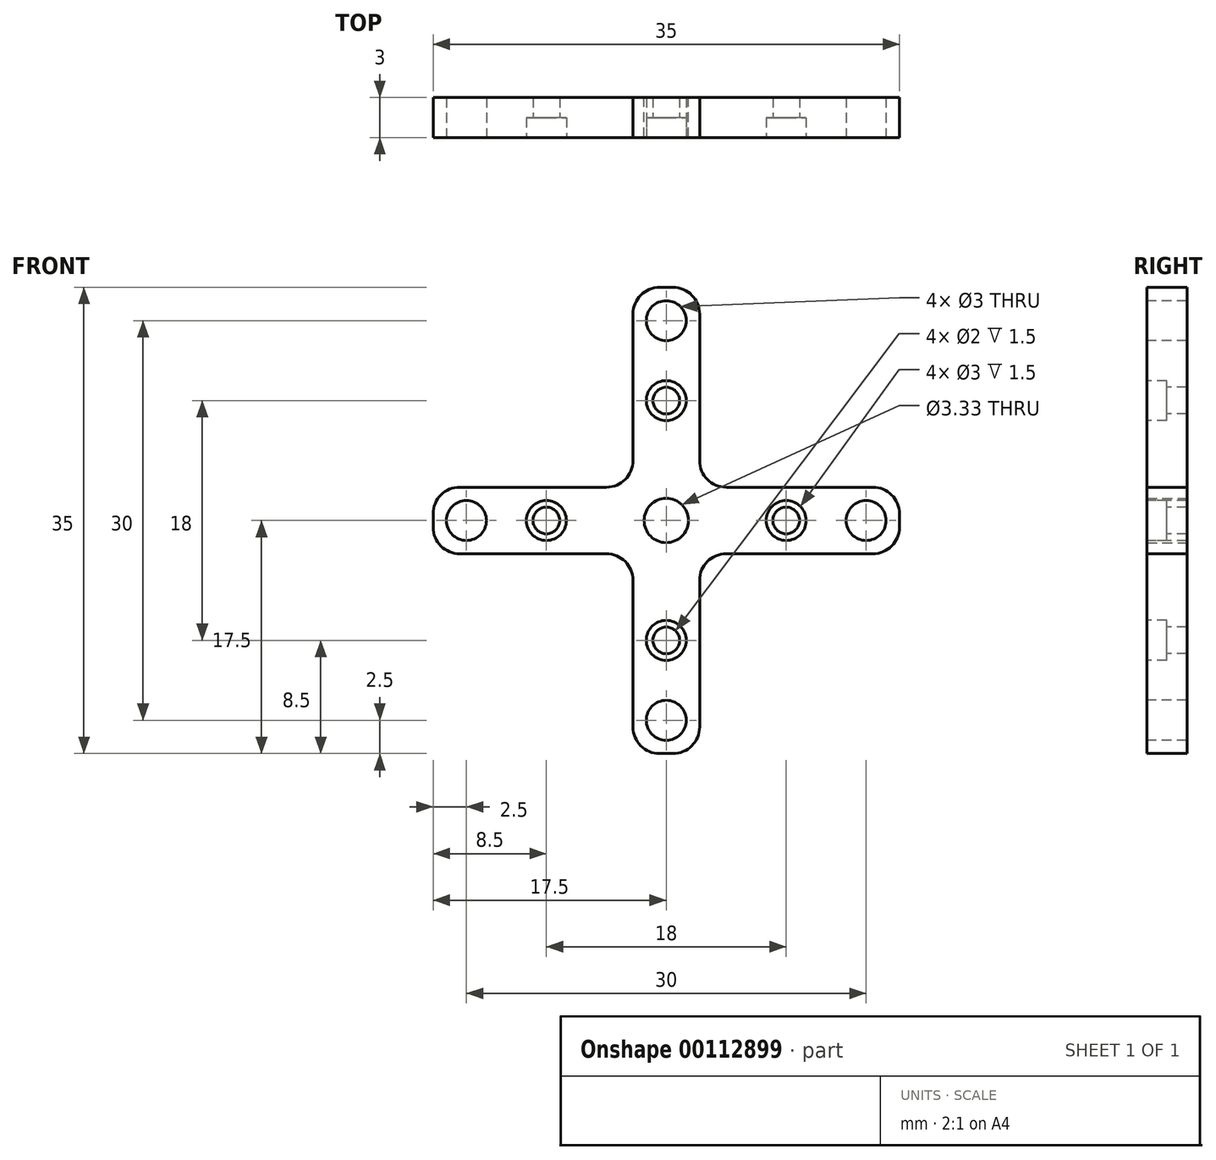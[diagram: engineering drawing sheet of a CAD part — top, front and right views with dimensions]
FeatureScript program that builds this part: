
annotation { "Feature Type Name" : "Feature", "Feature Type Description" : "" }
export const myFeature = defineFeature(function(context is Context, id is Id, definition is map)
    precondition{}
    {
        {
            var Q0;
            Q0=qCreatedBy(makeId("Front.planeOp"),FACE);
            var sketch = newSketch(context, id + "F0", { "sketchPlane" : qUnion([Q0])});
            skLineSegment(sketch, "E0.bottom", {"start": v(2.5, -17.5) * mm, "end": v(-2.5, -17.5) * mm});
            skLineSegment(sketch, "E0.top", {"start": v(2.5, 17.5) * mm, "end": v(-2.5, 17.5) * mm});
            skLineSegment(sketch, "E0.left", {"start": v(2.5, -17.5) * mm, "end": v(2.5, 17.5) * mm});
            skLineSegment(sketch, "E0.right", {"start": v(-2.5, -17.5) * mm, "end": v(-2.5, 17.5) * mm});
            skPoint(sketch, "E0.middle", {"position": v(0, 0) * mm});
            skLineSegment(sketch, "E1.bottom", {"start": v(17.5, -2.5) * mm, "end": v(-17.5, -2.5) * mm});
            skLineSegment(sketch, "E1.top", {"start": v(17.5, 2.5) * mm, "end": v(-17.5, 2.5) * mm});
            skLineSegment(sketch, "E1.left", {"start": v(17.5, -2.5) * mm, "end": v(17.5, 2.5) * mm});
            skLineSegment(sketch, "E1.right", {"start": v(-17.5, -2.5) * mm, "end": v(-17.5, 2.5) * mm});
            skCircle(sketch, "E2", {"center": v(0, 0) * mm, "radius": 1.66 * mm});
            skSolve(sketch);
        }
        {
            var Q0;
            Q0 = qSketchRegion(id + "F0", true);
            extrude(context, id + "F1", {"entities" : qUnion([Q0]), "depth" : 3 * mm});
        }
        {
            var Q0;
            Q0=makeQuery(id+"F1.opExtrude","SWEPT_EDGE",EDGE,{"disambiguationData":[OSD([sQuery(id+"F0.wireOp",EDGE,"E1.top"),sQuery(id+"F0.wireOp",EDGE,"E1.left")])]});
            var Q1;
            Q1=makeQuery(id+"F1.opExtrude","SWEPT_EDGE",EDGE,{"disambiguationData":[OSD([sQuery(id+"F0.wireOp",EDGE,"E1.bottom"),sQuery(id+"F0.wireOp",EDGE,"E1.left")])]});
            var Q2;
            Q2=makeQuery(id+"F1.opExtrude","SWEPT_EDGE",EDGE,{"disambiguationData":[OSD([sQuery(id+"F0.wireOp",EDGE,"E0.bottom"),sQuery(id+"F0.wireOp",EDGE,"E0.left")])]});
            var Q3;
            Q3=makeQuery(id+"F1.opExtrude","SWEPT_EDGE",EDGE,{"disambiguationData":[OSD([sQuery(id+"F0.wireOp",EDGE,"E1.top"),sQuery(id+"F0.wireOp",EDGE,"E1.right")])]});
            var Q4;
            Q4=makeQuery(id+"F1.opExtrude","SWEPT_EDGE",EDGE,{"disambiguationData":[OSD([sQuery(id+"F0.wireOp",EDGE,"E0.top"),sQuery(id+"F0.wireOp",EDGE,"E0.left")])]});
            var Q5;
            Q5=makeQuery(id+"F1.opExtrude","SWEPT_EDGE",EDGE,{"disambiguationData":[OSD([sQuery(id+"F0.wireOp",EDGE,"E0.top"),sQuery(id+"F0.wireOp",EDGE,"E0.right")])]});
            var Q6;
            Q6=makeQuery(id+"F1.opExtrude","SWEPT_EDGE",EDGE,{"disambiguationData":[OSD([sQuery(id+"F0.wireOp",EDGE,"E0.bottom"),sQuery(id+"F0.wireOp",EDGE,"E0.right")])]});
            var Q7;
            Q7=makeQuery(id+"F1.opExtrude","SWEPT_EDGE",EDGE,{"disambiguationData":[OSD([sQuery(id+"F0.wireOp",EDGE,"E1.bottom"),sQuery(id+"F0.wireOp",EDGE,"E1.right")])]});
            var Q8;
            Q8=makeQuery(id+"F1.opExtrude","SWEPT_EDGE",EDGE,{"disambiguationData":[OSD([sQuery(id+"F0.wireOp",EDGE,"E0.right"),sQuery(id+"F0.wireOp",EDGE,"E1.top")])]});
            var Q9;
            Q9=makeQuery(id+"F1.opExtrude","SWEPT_EDGE",EDGE,{"disambiguationData":[OSD([sQuery(id+"F0.wireOp",EDGE,"E0.left"),sQuery(id+"F0.wireOp",EDGE,"E1.bottom")])]});
            var Q10;
            Q10=makeQuery(id+"F1.opExtrude","SWEPT_EDGE",EDGE,{"disambiguationData":[OSD([sQuery(id+"F0.wireOp",EDGE,"E0.left"),sQuery(id+"F0.wireOp",EDGE,"E1.top")])]});
            var Q11;
            Q11=makeQuery(id+"F1.opExtrude","SWEPT_EDGE",EDGE,{"disambiguationData":[OSD([sQuery(id+"F0.wireOp",EDGE,"E0.right"),sQuery(id+"F0.wireOp",EDGE,"E1.bottom")])]});
            fillet(context, id + "F2", {"entities" : qUnion([Q0, Q1, Q2, Q3, Q4, Q5, Q6, Q7, Q8, Q9, Q10, Q11]), "radius" : 2 * mm, "tangentPropagation" : true, "allowEdgeOverflow" : false});
        }
        {
            var Q0;
            Q0=makeQuery(id+"F1.opExtrude","CAP_FACE",FACE,{"disambiguationData":[OSD([sQuery(id+"F0.wireOp",EDGE,"E0.bottom"),sQuery(id+"F0.wireOp",EDGE,"E0.top"),sQuery(id+"F0.wireOp",EDGE,"E0.left"),sQuery(id+"F0.wireOp",EDGE,"E0.right"),sQuery(id+"F0.wireOp",EDGE,"E1.bottom"),sQuery(id+"F0.wireOp",EDGE,"E1.top"),sQuery(id+"F0.wireOp",EDGE,"E1.left"),sQuery(id+"F0.wireOp",EDGE,"E1.right"),sQuery(id+"F0.wireOp",EDGE,"E2")])],"isStart":false});
            var sketch = newSketch(context, id + "F3", { "sketchPlane" : qUnion([Q0])});
            skCircle(sketch, "E3", {"center": v(-15, 0) * mm, "radius": 1.5 * mm});
            skCircle(sketch, "E4.MirrorC", {"center": v(15, 0) * mm, "radius": 1.5 * mm});
            skCircle(sketch, "E5", {"center": v(0, -15) * mm, "radius": 1.5 * mm});
            skCircle(sketch, "E6.MirrorC", {"center": v(0, 15) * mm, "radius": 1.5 * mm});
            skSolve(sketch);
        }
        {
            var Q0;
            Q0=sQuery(id+"F3.wireOp",VERTEX,"E3.center");
            var Q1;
            Q1=sQuery(id+"F3.wireOp",VERTEX,"E6.MirrorC.center");
            var Q2;
            Q2=sQuery(id+"F3.wireOp",VERTEX,"E4.MirrorC.center");
            var Q3;
            Q3=sQuery(id+"F3.wireOp",VERTEX,"E5.center");
            var Q4;
            Q4=makeQuery(id+"F1.opExtrude","SWEPT_BODY",BODY,{"disambiguationData":[OSD([sQuery(id+"F0.wireOp",EDGE,"E0.bottom"),sQuery(id+"F0.wireOp",EDGE,"E0.top"),sQuery(id+"F0.wireOp",EDGE,"E0.left"),sQuery(id+"F0.wireOp",EDGE,"E0.right"),sQuery(id+"F0.wireOp",EDGE,"E1.bottom"),sQuery(id+"F0.wireOp",EDGE,"E1.top"),sQuery(id+"F0.wireOp",EDGE,"E1.left"),sQuery(id+"F0.wireOp",EDGE,"E1.right"),sQuery(id+"F0.wireOp",EDGE,"E2")])]});
            hole(context, id + "F4", {"style" : HoleStyle.SIMPLE, "endStyle" : HoleEndStyle.THROUGH, "holeDiameter" : 3 * mm, "locations" : qUnion([Q0, Q1, Q2, Q3]), "scope" : qUnion([Q4]), "isTappedThrough" : true});
        }
        {
            var Q0;
            Q0=makeQuery(id+"F1.opExtrude","CAP_FACE",FACE,{"disambiguationData":[OSD([sQuery(id+"F0.wireOp",EDGE,"E0.bottom"),sQuery(id+"F0.wireOp",EDGE,"E0.top"),sQuery(id+"F0.wireOp",EDGE,"E0.left"),sQuery(id+"F0.wireOp",EDGE,"E0.right"),sQuery(id+"F0.wireOp",EDGE,"E1.bottom"),sQuery(id+"F0.wireOp",EDGE,"E1.top"),sQuery(id+"F0.wireOp",EDGE,"E1.left"),sQuery(id+"F0.wireOp",EDGE,"E1.right"),sQuery(id+"F0.wireOp",EDGE,"E2")])],"isStart":false});
            var sketch = newSketch(context, id + "F5", { "sketchPlane" : qUnion([Q0])});
            skCircle(sketch, "E7", {"center": v(0, 9) * mm, "radius": 1 * mm});
            skCircle(sketch, "E8", {"center": v(9, 0) * mm, "radius": 1 * mm});
            skCircle(sketch, "E9.MirrorC", {"center": v(0, -9) * mm, "radius": 1 * mm});
            skCircle(sketch, "E10.MirrorC", {"center": v(-9, 0) * mm, "radius": 1 * mm});
            skSolve(sketch);
        }
        {
            var Q0;
            Q0=sQuery(id+"F5.wireOp",VERTEX,"E7.center");
            var Q1;
            Q1=sQuery(id+"F5.wireOp",VERTEX,"E8.center");
            var Q2;
            Q2=sQuery(id+"F5.wireOp",VERTEX,"E9.MirrorC.center");
            var Q3;
            Q3=sQuery(id+"F5.wireOp",VERTEX,"E10.MirrorC.center");
            var Q4;
            Q4=makeQuery(id+"F1.opExtrude","SWEPT_BODY",BODY,{"disambiguationData":[OSD([sQuery(id+"F0.wireOp",EDGE,"E0.bottom"),sQuery(id+"F0.wireOp",EDGE,"E0.top"),sQuery(id+"F0.wireOp",EDGE,"E0.left"),sQuery(id+"F0.wireOp",EDGE,"E0.right"),sQuery(id+"F0.wireOp",EDGE,"E1.bottom"),sQuery(id+"F0.wireOp",EDGE,"E1.top"),sQuery(id+"F0.wireOp",EDGE,"E1.left"),sQuery(id+"F0.wireOp",EDGE,"E1.right"),sQuery(id+"F0.wireOp",EDGE,"E2")])]});
            hole(context, id + "F6", {"style" : HoleStyle.C_BORE, "endStyle" : HoleEndStyle.THROUGH, "holeDiameter" : 2 * mm, "cBoreDiameter" : 3 * mm, "cBoreDepth" : 1.5 * mm, "locations" : qUnion([Q0, Q1, Q2, Q3]), "scope" : qUnion([Q4]), "isTappedThrough" : true});
        }
    });
